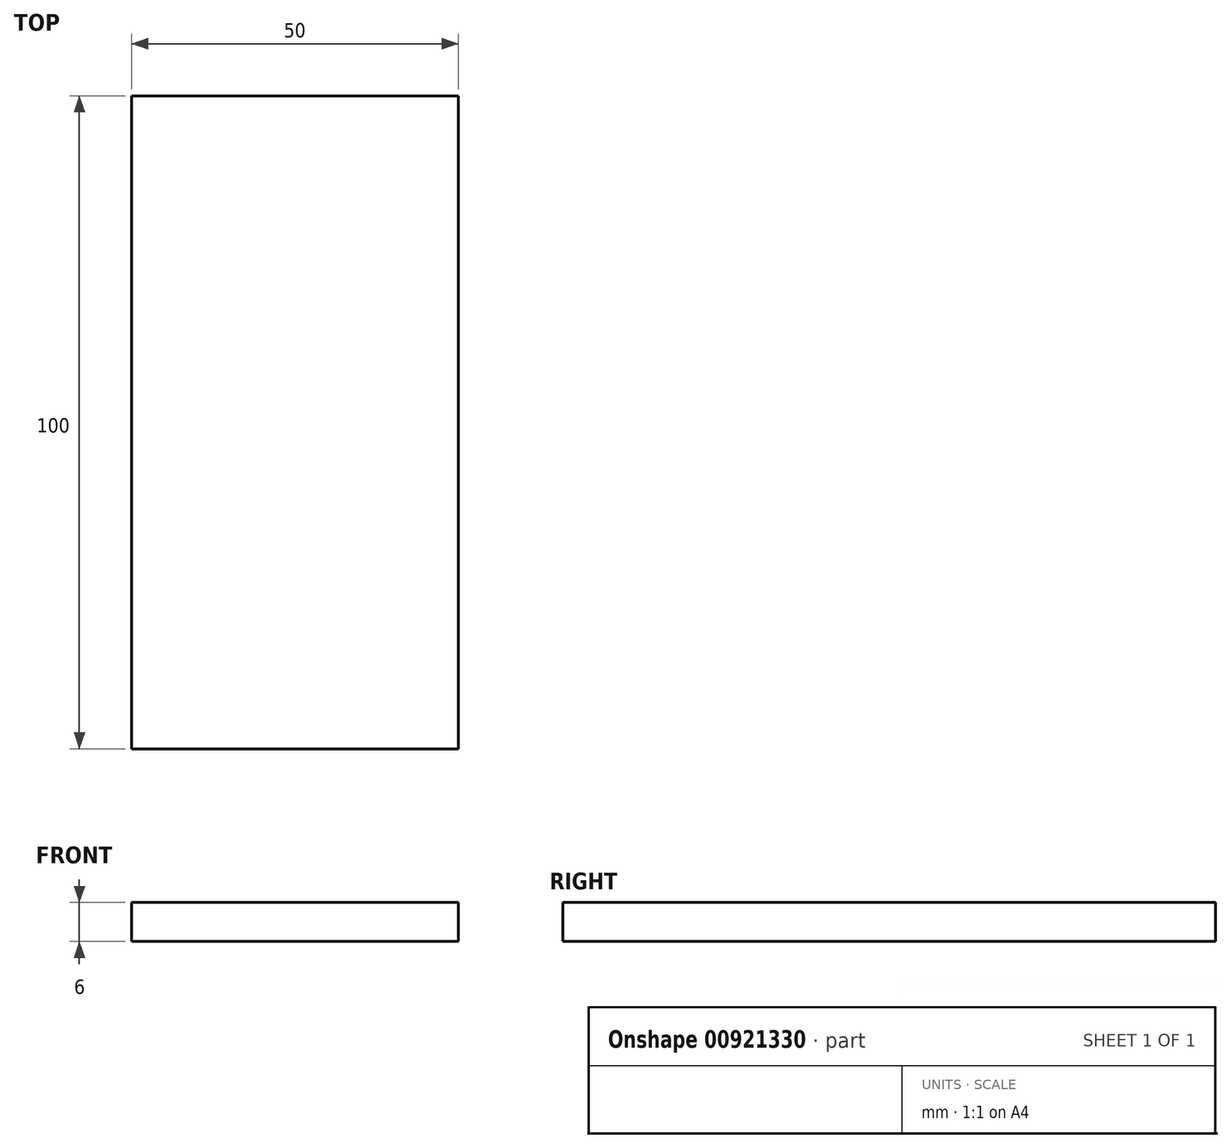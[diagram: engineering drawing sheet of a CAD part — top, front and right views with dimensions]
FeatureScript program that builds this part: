
annotation { "Feature Type Name" : "Feature", "Feature Type Description" : "" }
export const myFeature = defineFeature(function(context is Context, id is Id, definition is map)
    precondition{}
    {
        {
            var Q0;
            Q0=qCreatedBy(makeId("Top.planeOp"),FACE);
            var sketch = newSketch(context, id + "F0", { "sketchPlane" : qUnion([Q0])});
            skLineSegment(sketch, "E0.bottom", {"start": v(-25, 50) * mm, "end": v(25, 50) * mm});
            skLineSegment(sketch, "E0.top", {"start": v(-25, -50) * mm, "end": v(25, -50) * mm});
            skLineSegment(sketch, "E0.left", {"start": v(-25, 50) * mm, "end": v(-25, -50) * mm});
            skLineSegment(sketch, "E0.right", {"start": v(25, 50) * mm, "end": v(25, -50) * mm});
            skPoint(sketch, "E0.middle", {"position": v(0, 0) * mm});
            skSolve(sketch);
        }
        {
            var Q0;
            Q0 = qSketchRegion(id + "F0", true);
            extrude(context, id + "F1", {"entities" : qUnion([Q0]), "depth" : 6 * mm, "offsetDistance" : 25 * mm});
        }
    });
